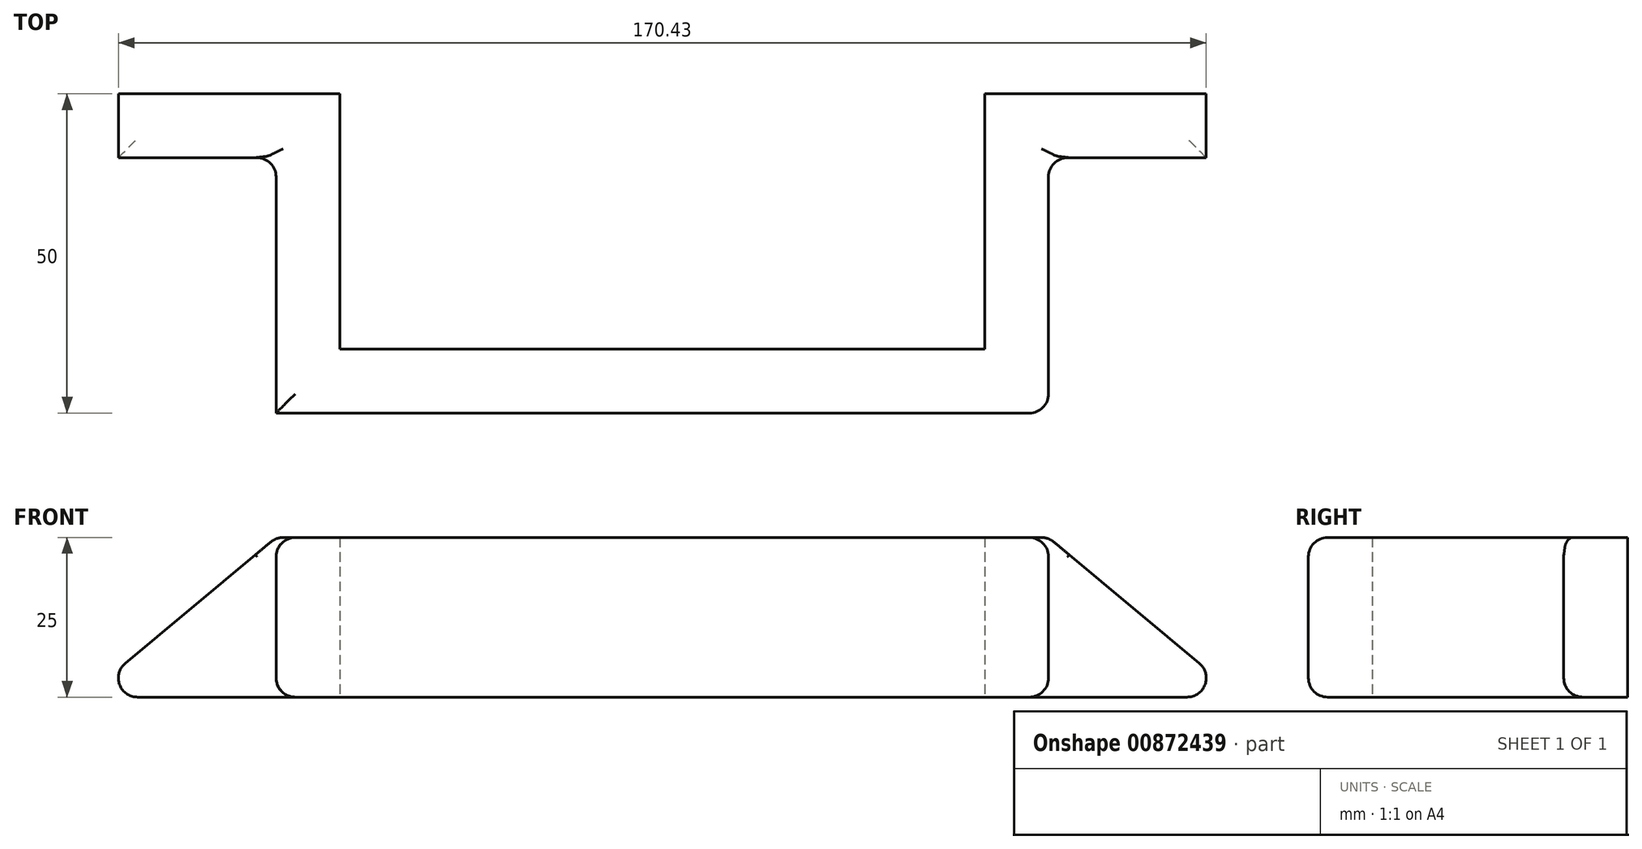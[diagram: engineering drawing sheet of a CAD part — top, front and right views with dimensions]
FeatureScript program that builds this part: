
annotation { "Feature Type Name" : "Feature", "Feature Type Description" : "" }
export const myFeature = defineFeature(function(context is Context, id is Id, definition is map)
    precondition{}
    {
        {
            var Q0;
            Q0=qCreatedBy(makeId("Top.planeOp"),FACE);
            var sketch = newSketch(context, id + "F0", { "sketchPlane" : qUnion([Q0])});
            skLineSegment(sketch, "E0", {"start": v(-53.28, -40) * mm, "end": v(47.72, -40) * mm});
            skLineSegment(sketch, "E1", {"start": v(47.72, -40) * mm, "end": v(47.72, 0) * mm});
            skLineSegment(sketch, "E2", {"start": v(47.72, 0) * mm, "end": v(87.72, 0) * mm});
            skLineSegment(sketch, "E3", {"start": v(-53.28, -40) * mm, "end": v(-53.28, 0) * mm});
            skLineSegment(sketch, "E4", {"start": v(-53.28, 0) * mm, "end": v(-93.28, 0) * mm});
            skLineSegment(sketch, "E5", {"start": v(-93.28, 0) * mm, "end": v(-93.28, -10) * mm});
            skLineSegment(sketch, "E6", {"start": v(-53.28, -40) * mm, "end": v(-63.28, -40) * mm});
            skLineSegment(sketch, "E7", {"start": v(-93.28, -10) * mm, "end": v(-53.28, -10) * mm});
            skLineSegment(sketch, "E8", {"start": v(-63.28, -40) * mm, "end": v(-63.28, 0) * mm});
            skLineSegment(sketch, "E9", {"start": v(-63.28, -40) * mm, "end": v(-63.28, -50) * mm});
            skLineSegment(sketch, "E10", {"start": v(47.72, -40) * mm, "end": v(57.72, -40) * mm});
            skLineSegment(sketch, "E11", {"start": v(57.72, -40) * mm, "end": v(57.72, -50) * mm});
            skLineSegment(sketch, "E12", {"start": v(-63.28, -50) * mm, "end": v(57.72, -50) * mm});
            skLineSegment(sketch, "E13", {"start": v(87.72, 0) * mm, "end": v(87.72, -10) * mm});
            skLineSegment(sketch, "E14", {"start": v(87.72, -10) * mm, "end": v(57.72, -10) * mm});
            skLineSegment(sketch, "E15", {"start": v(57.72, -40) * mm, "end": v(57.72, -10) * mm});
            skSolve(sketch);
        }
        {
            var Q0;
            {var subQ0=sQuery(id+"F0.wireOp",EDGE,"E5");Q0=makeQuery(id+"F0.imprint","IMPRINT",FACE,{"disambiguationData":[TD([[makeQuery(id+"F0.imprint","IMPRINT",EDGE,{"derivedFrom":subQ0}),1.0]])]});}
            var Q1;
            {var subQ0=sQuery(id+"F0.wireOp",EDGE,"E6");Q1=makeQuery(id+"F0.imprint","IMPRINT",FACE,{"disambiguationData":[TD([[makeQuery(id+"F0.imprint","IMPRINT",EDGE,{"derivedFrom":subQ0}),-1.0]])]});}
            var Q2;
            Q2=makeQuery(id+"F0.imprint","IMPRINT",FACE,{"disambiguationData":[TD([[makeQuery(id+"F0.imprint","IMPRINT",EDGE,{"derivedFrom":sQuery(id+"F0.wireOp",EDGE,"E1")}),-1.0]])]});
            var Q3;
            {var subQ0=sQuery(id+"F0.wireOp",EDGE,"E4");var subQ1=sQuery(id+"F0.wireOp",EDGE,"E3");var subQ2=makeQuery(id+"F0.imprint","INTERSECT",VERTEX,{"derivedFrom":[subQ1,subQ0]});Q3=makeQuery(id+"F0.imprint","IMPRINT",FACE,{"disambiguationData":[TD([[makeQuery(id+"F0.imprint","IMPRINT",EDGE,{"disambiguationData":[TD([[subQ2,1.0]])],"derivedFrom":subQ1}),1.0]])]});}
            var Q4;
            Q4=makeQuery(id+"F0.imprint","IMPRINT",FACE,{"disambiguationData":[TD([[makeQuery(id+"F0.imprint","IMPRINT",EDGE,{"derivedFrom":sQuery(id+"F0.wireOp",EDGE,"E0")}),-1.0]])]});
            extrude(context, id + "F1", {"entities" : qUnion([Q0, Q1, Q2, Q3, Q4]), "depth" : 25 * mm, "offsetDistance" : 25 * mm});
        }
        {
            var Q0;
            Q0=makeQuery(id+"F1.opExtrude","SWEPT_FACE",FACE,{"disambiguationData":[OSD([sQuery(id+"F0.wireOp",EDGE,"E14")])]});
            var sketch = newSketch(context, id + "F2", { "sketchPlane" : qUnion([Q0])});
            skLineSegment(sketch, "E16", {"start": v(57.72, 0) * mm, "end": v(87.72, 25) * mm});
            skLineSegment(sketch, "E17", {"start": v(87.72, 0) * mm, "end": v(57.72, 25) * mm});
            skCircle(sketch, "E18", {"center": v(72.72, 12.5) * mm, "radius": 2 * mm});
            skLineSegment(sketch, "E19", {"start": v(-93.25, 0) * mm, "end": v(-63.03, 25.18) * mm});
            skSolve(sketch);
        }
        {
            var Q0;
            {var subQ0=sQuery(id+"F2.wireOp",EDGE,"E17");var subQ1=sQuery(id+"F2.wireOp",EDGE,"E16");var subQ2=makeQuery(id+"F2.imprint","INTERSECT",VERTEX,{"derivedFrom":[subQ1,subQ0]});Q0=makeQuery(id+"F2.imprint","IMPRINT",FACE,{"disambiguationData":[TD([[makeQuery(id+"F2.imprint","IMPRINT",EDGE,{"disambiguationData":[TD([[subQ2,-1.0]])],"derivedFrom":subQ1}),-1.0]])]});}
            var Q1;
            {var subQ0=sQuery(id+"F2.wireOp",EDGE,"E17");var subQ1=sQuery(id+"F2.wireOp",EDGE,"E16");var subQ2=makeQuery(id+"F2.imprint","INTERSECT",VERTEX,{"derivedFrom":[subQ1,subQ0]});Q1=makeQuery(id+"F2.imprint","IMPRINT",FACE,{"disambiguationData":[TD([[makeQuery(id+"F2.imprint","IMPRINT",EDGE,{"disambiguationData":[TD([[subQ2,-1.0]])],"derivedFrom":subQ1}),1.0]])]});}
            var Q2;
            {var subQ0=sQuery(id+"F2.wireOp",EDGE,"E18");var subQ1=sQuery(id+"F2.wireOp",EDGE,"E16");var subQ2=makeQuery(id+"F2.imprint","INTERSECT",VERTEX,{"disambiguationData":[OD(0.0)],"derivedFrom":[subQ1,subQ0]});Q2=makeQuery(id+"F2.imprint","IMPRINT",FACE,{"disambiguationData":[TD([[makeQuery(id+"F2.imprint","IMPRINT",EDGE,{"disambiguationData":[TD([[subQ2,-1.0]])],"derivedFrom":subQ1}),1.0]])]});}
            var Q3;
            {var subQ0=sQuery(id+"F2.wireOp",EDGE,"E18");var subQ1=sQuery(id+"F2.wireOp",EDGE,"E16");var subQ2=makeQuery(id+"F2.imprint","INTERSECT",VERTEX,{"disambiguationData":[OD(0.0)],"derivedFrom":[subQ1,subQ0]});Q3=makeQuery(id+"F2.imprint","IMPRINT",FACE,{"disambiguationData":[TD([[makeQuery(id+"F2.imprint","IMPRINT",EDGE,{"disambiguationData":[TD([[subQ2,-1.0]])],"derivedFrom":subQ1}),-1.0]])]});}
            var Q4;
            Q4=sQuery(id+"F2.wireOp",EDGE,"E18");
            extrude(context, id + "F3", {"entities" : qUnion([Q0, Q1, Q2, Q3]), "operationType" : NewBodyOperationType.REMOVE, "surfaceEntities" : qUnion([Q4]), "oppositeDirection" : true, "depth" : 25 * mm, "offsetDistance" : 25 * mm});
        }
        {
            var Q0;
            Q0=makeQuery(id+"F1.opExtrude","SWEPT_FACE",FACE,{"disambiguationData":[OSD([sQuery(id+"F0.wireOp",EDGE,"E7")])]});
            var sketch = newSketch(context, id + "F4", { "sketchPlane" : qUnion([Q0])});
            skLineSegment(sketch, "E20", {"start": v(-63.28, 0) * mm, "end": v(-93.28, 25) * mm});
            skLineSegment(sketch, "E21", {"start": v(-93.28, 0) * mm, "end": v(-63.28, 25) * mm});
            skCircle(sketch, "E22", {"center": v(-78.28, 12.5) * mm, "radius": 2 * mm});
            skSolve(sketch);
        }
        {
            var Q0;
            {var subQ0=sQuery(id+"F4.wireOp",EDGE,"E22");var subQ1=sQuery(id+"F4.wireOp",EDGE,"E20");var subQ2=makeQuery(id+"F4.imprint","INTERSECT",VERTEX,{"disambiguationData":[OD(0.0)],"derivedFrom":[subQ1,subQ0]});Q0=makeQuery(id+"F4.imprint","IMPRINT",FACE,{"disambiguationData":[TD([[makeQuery(id+"F4.imprint","IMPRINT",EDGE,{"disambiguationData":[TD([[subQ2,-1.0]])],"derivedFrom":subQ1}),1.0]])]});}
            var Q1;
            {var subQ0=sQuery(id+"F4.wireOp",EDGE,"E22");var subQ1=sQuery(id+"F4.wireOp",EDGE,"E20");var subQ2=makeQuery(id+"F4.imprint","INTERSECT",VERTEX,{"disambiguationData":[OD(0.0)],"derivedFrom":[subQ1,subQ0]});Q1=makeQuery(id+"F4.imprint","IMPRINT",FACE,{"disambiguationData":[TD([[makeQuery(id+"F4.imprint","IMPRINT",EDGE,{"disambiguationData":[TD([[subQ2,-1.0]])],"derivedFrom":subQ1}),-1.0]])]});}
            var Q2;
            {var subQ0=sQuery(id+"F4.wireOp",EDGE,"E21");var subQ1=sQuery(id+"F4.wireOp",EDGE,"E20");var subQ2=makeQuery(id+"F4.imprint","INTERSECT",VERTEX,{"derivedFrom":[subQ1,subQ0]});Q2=makeQuery(id+"F4.imprint","IMPRINT",FACE,{"disambiguationData":[TD([[makeQuery(id+"F4.imprint","IMPRINT",EDGE,{"disambiguationData":[TD([[subQ2,-1.0]])],"derivedFrom":subQ1}),-1.0]])]});}
            var Q3;
            {var subQ0=sQuery(id+"F4.wireOp",EDGE,"E21");var subQ1=sQuery(id+"F4.wireOp",EDGE,"E20");var subQ2=makeQuery(id+"F4.imprint","INTERSECT",VERTEX,{"derivedFrom":[subQ1,subQ0]});Q3=makeQuery(id+"F4.imprint","IMPRINT",FACE,{"disambiguationData":[TD([[makeQuery(id+"F4.imprint","IMPRINT",EDGE,{"disambiguationData":[TD([[subQ2,-1.0]])],"derivedFrom":subQ1}),1.0]])]});}
            var Q4;
            Q4=sQuery(id+"F4.wireOp",EDGE,"E22");
            extrude(context, id + "F5", {"entities" : qUnion([Q0, Q1, Q2, Q3]), "operationType" : NewBodyOperationType.REMOVE, "surfaceEntities" : qUnion([Q4]), "oppositeDirection" : true, "depth" : 25 * mm, "offsetDistance" : 25 * mm});
        }
        {
            var Q0;
            Q0=makeQuery(id+"F1.opExtrude","SWEPT_EDGE",EDGE,{"disambiguationData":[OSD([sQuery(id+"F0.wireOp",EDGE,"E5"),sQuery(id+"F0.wireOp",EDGE,"E7")])]});
            var Q1;
            Q1=makeQuery(id+"F1.opExtrude","CAP_EDGE",EDGE,{"disambiguationData":[OSD([sQuery(id+"F0.wireOp",EDGE,"E7")])],"isStart":true});
            var Q2;
            Q2=makeQuery(id+"F1.opExtrude","CAP_EDGE",EDGE,{"disambiguationData":[OSD([sQuery(id+"F0.wireOp",EDGE,"E8"),sQuery(id+"F0.wireOp",EDGE,"E9")])],"isStart":true});
            var Q3;
            Q3=makeQuery(id+"F1.opExtrude","CAP_EDGE",EDGE,{"disambiguationData":[OSD([sQuery(id+"F0.wireOp",EDGE,"E8"),sQuery(id+"F0.wireOp",EDGE,"E9")])],"isStart":false});
            var Q4;
            Q4=makeQuery(id+"F1.opExtrude","SWEPT_EDGE",EDGE,{"disambiguationData":[OSD([sQuery(id+"F0.wireOp",EDGE,"E7"),sQuery(id+"F0.wireOp",EDGE,"E8")])]});
            var Q5;
            Q5=makeQuery(id+"F1.opExtrude","CAP_EDGE",EDGE,{"disambiguationData":[OSD([sQuery(id+"F0.wireOp",EDGE,"E7")])],"isStart":false});
            var Q6;
            Q6=makeQuery(id+"F1.opExtrude","CAP_EDGE",EDGE,{"disambiguationData":[OSD([sQuery(id+"F0.wireOp",EDGE,"E12")])],"isStart":true});
            var Q7;
            Q7=makeQuery(id+"F1.opExtrude","CAP_EDGE",EDGE,{"disambiguationData":[OSD([sQuery(id+"F0.wireOp",EDGE,"E12")])],"isStart":false});
            var Q8;
            Q8=makeQuery(id+"F1.opExtrude","CAP_EDGE",EDGE,{"disambiguationData":[OSD([sQuery(id+"F0.wireOp",EDGE,"E5")])],"isStart":true});
            var Q9;
            Q9=makeQuery(id+"F1.opExtrude","SWEPT_EDGE",EDGE,{"disambiguationData":[OSD([sQuery(id+"F0.wireOp",EDGE,"E11"),sQuery(id+"F0.wireOp",EDGE,"E12")])]});
            var Q10;
            Q10=makeQuery(id+"F1.opExtrude","CAP_EDGE",EDGE,{"disambiguationData":[OSD([sQuery(id+"F0.wireOp",EDGE,"E11"),sQuery(id+"F0.wireOp",EDGE,"E15")])],"isStart":true});
            var Q11;
            Q11=makeQuery(id+"F1.opExtrude","CAP_EDGE",EDGE,{"disambiguationData":[OSD([sQuery(id+"F0.wireOp",EDGE,"E14")])],"isStart":true});
            var Q12;
            Q12=makeQuery(id+"F1.opExtrude","CAP_EDGE",EDGE,{"disambiguationData":[OSD([sQuery(id+"F0.wireOp",EDGE,"E14")])],"isStart":false});
            var Q13;
            Q13=makeQuery(id+"F1.opExtrude","SWEPT_EDGE",EDGE,{"disambiguationData":[OSD([sQuery(id+"F0.wireOp",EDGE,"E13"),sQuery(id+"F0.wireOp",EDGE,"E14")])]});
            var Q14;
            Q14=makeQuery(id+"F1.opExtrude","CAP_EDGE",EDGE,{"disambiguationData":[OSD([sQuery(id+"F0.wireOp",EDGE,"E13")])],"isStart":true});
            var Q15;
            Q15=makeQuery(id+"F1.opExtrude","CAP_EDGE",EDGE,{"disambiguationData":[OSD([sQuery(id+"F0.wireOp",EDGE,"E13")])],"isStart":false});
            var Q16;
            Q16=makeQuery(id+"F1.opExtrude","CAP_EDGE",EDGE,{"disambiguationData":[OSD([sQuery(id+"F0.wireOp",EDGE,"E11"),sQuery(id+"F0.wireOp",EDGE,"E15")])],"isStart":false});
            var Q17;
            Q17=makeQuery(id+"F1.opExtrude","SWEPT_EDGE",EDGE,{"disambiguationData":[OSD([sQuery(id+"F0.wireOp",EDGE,"E14"),sQuery(id+"F0.wireOp",EDGE,"E15")])]});
            var Q18;
            Q18=makeQuery(id+"F1.opExtrude","CAP_EDGE",EDGE,{"disambiguationData":[OSD([sQuery(id+"F0.wireOp",EDGE,"E5")])],"isStart":false});
            fillet(context, id + "F6", {"entities" : qUnion([Q0, Q1, Q2, Q3, Q4, Q5, Q6, Q7, Q8, Q9, Q10, Q11, Q12, Q13, Q14, Q15, Q16, Q17, Q18]), "radius" : 3 * mm, "tangentPropagation" : true, "allowEdgeOverflow" : false});
        }
    });
